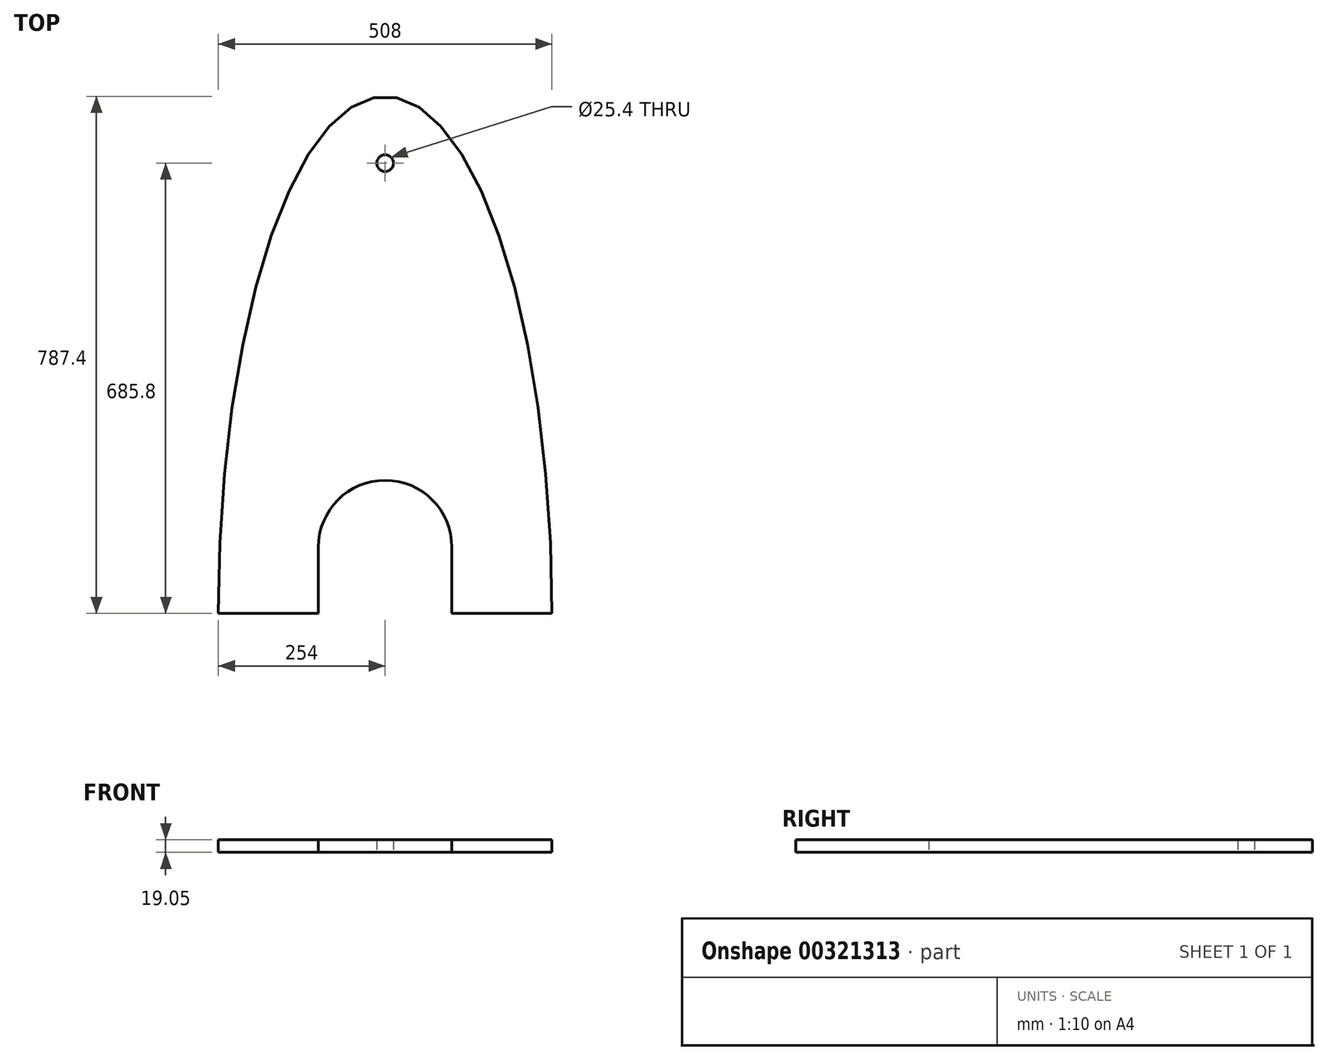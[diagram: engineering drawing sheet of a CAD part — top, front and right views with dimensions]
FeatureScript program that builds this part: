
annotation { "Feature Type Name" : "Feature", "Feature Type Description" : "" }
export const myFeature = defineFeature(function(context is Context, id is Id, definition is map)
    precondition{}
    {
        {
            var Q0;
            Q0=qCreatedBy(makeId("Top.planeOp"),FACE);
            var sketch = newSketch(context, id + "F0", { "sketchPlane" : qUnion([Q0])});
            skEllipticalArc(sketch, "E0", {});
            skLineSegment(sketch, "E1", {"start": v(-254, 0) * mm, "end": v(-101.6, 0) * mm});
            skLineSegment(sketch, "E2.trimOffspring", {"start": v(101.6, 0) * mm, "end": v(254, 0) * mm});
            skCircle(sketch, "E3", {"center": v(0, 685.8) * mm, "radius": 12.7 * mm});
            skLineSegment(sketch, "E4", {"start": v(-101.6, 0) * mm, "end": v(-101.6, 101.05) * mm});
            skLineSegment(sketch, "E5", {"start": v(101.6, 101.05) * mm, "end": v(101.6, 0) * mm});
            skArc(sketch, "E6", {"start": v(101.6, 101.05) * mm, "mid": v(0, 202.65) * mm, "end": v(-101.6, 101.05) * mm});
            const initialGuessF0  = {"E0": [0, 0, 0, -1, 0.7874, 0.254, 1.5707963267948966, 4.71238898038469]};
            skSetInitialGuess(sketch, initialGuessF0);
            skSolve(sketch);
        }
        {
            var Q0;
            Q0 = qSketchRegion(id + "F0", true);
            extrude(context, id + "F1", {"entities" : qUnion([Q0]), "depth" : 19.05 * mm});
        }
    });
